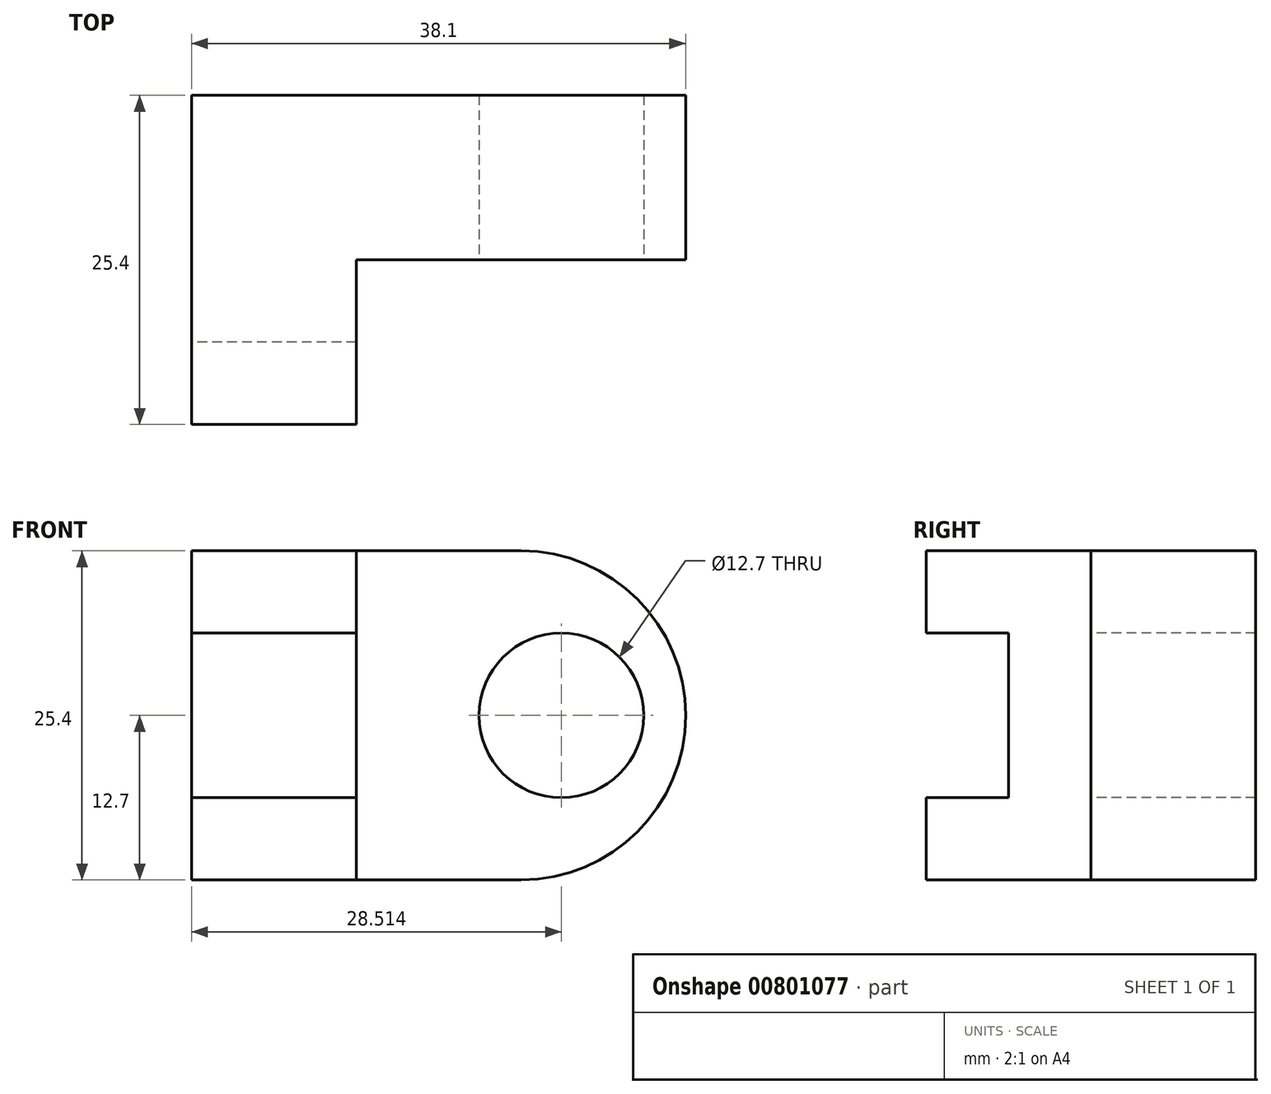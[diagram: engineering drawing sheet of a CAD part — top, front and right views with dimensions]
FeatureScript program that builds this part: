
annotation { "Feature Type Name" : "Feature", "Feature Type Description" : "" }
export const myFeature = defineFeature(function(context is Context, id is Id, definition is map)
    precondition{}
    {
        {
            var Q0;
            Q0=qCreatedBy(makeId("Front.planeOp"),FACE);
            var sketch = newSketch(context, id + "F0", { "sketchPlane" : qUnion([Q0])});
            skLineSegment(sketch, "E0", {"start": v(0, 0) * mm, "end": v(12.7, 0) * mm});
            skLineSegment(sketch, "E1", {"start": v(0, 0) * mm, "end": v(0, 25.4) * mm});
            skLineSegment(sketch, "E2", {"start": v(12.7, 0) * mm, "end": v(12.7, 25.4) * mm});
            skLineSegment(sketch, "E3", {"start": v(12.7, 25.4) * mm, "end": v(0, 25.4) * mm});
            skSolve(sketch);
        }
        {
            var Q0;
            Q0 = qSketchRegion(id + "F0", true);
            extrude(context, id + "F1", {"entities" : qUnion([Q0]), "depth" : 25.4 * mm, "offsetDistance" : 25.4 * mm});
        }
        {
            var Q0;
            Q0=makeQuery(id+"F1.opExtrude","SWEPT_FACE",FACE,{"disambiguationData":[OSD([sQuery(id+"F0.wireOp",EDGE,"E2")])]});
            var sketch = newSketch(context, id + "F2", { "sketchPlane" : qUnion([Q0])});
            skLineSegment(sketch, "E4", {"start": v(0, 0) * mm, "end": v(-12.7, 0) * mm});
            skLineSegment(sketch, "E5", {"start": v(-12.7, 0) * mm, "end": v(-12.7, 25.4) * mm});
            skLineSegment(sketch, "E6", {"start": v(0, 0) * mm, "end": v(0, 25.4) * mm});
            skLineSegment(sketch, "E7", {"start": v(-12.7, 25.4) * mm, "end": v(0, 25.4) * mm});
            skSolve(sketch);
        }
        {
            var Q0;
            Q0 = qSketchRegion(id + "F2", true);
            extrude(context, id + "F3", {"entities" : qUnion([Q0]), "operationType" : NewBodyOperationType.ADD, "depth" : 25.4 * mm, "offsetDistance" : 25.4 * mm});
        }
        {
            var Q0;
            Q0=makeQuery(id+"F1.opExtrude","CAP_FACE",FACE,{"disambiguationData":[OSD([sQuery(id+"F0.wireOp",EDGE,"E0"),sQuery(id+"F0.wireOp",EDGE,"E1"),sQuery(id+"F0.wireOp",EDGE,"E2"),sQuery(id+"F0.wireOp",EDGE,"E3")])],"isStart":false});
            var sketch = newSketch(context, id + "F4", { "sketchPlane" : qUnion([Q0])});
            skLineSegment(sketch, "E8", {"start": v(12.7, 0) * mm, "end": v(12.7, 6.35) * mm});
            skLineSegment(sketch, "E9", {"start": v(12.7, 6.35) * mm, "end": v(0, 6.35) * mm});
            skLineSegment(sketch, "E10", {"start": v(0, 6.35) * mm, "end": v(0, 0) * mm});
            skLineSegment(sketch, "E11", {"start": v(12.7, 6.35) * mm, "end": v(12.7, 19.05) * mm});
            skLineSegment(sketch, "E12", {"start": v(12.7, 19.05) * mm, "end": v(0, 19.05) * mm});
            skSolve(sketch);
        }
        {
            var Q0;
            {var subQ0=sQuery(id+"F4.wireOp",EDGE,"E9");Q0=makeQuery(id+"F4.imprint","IMPRINT",FACE,{"disambiguationData":[TD([[makeQuery(id+"F4.imprint","IMPRINT",EDGE,{"derivedFrom":subQ0}),-1.0]])]});}
            extrude(context, id + "F5", {"entities" : qUnion([Q0]), "operationType" : NewBodyOperationType.REMOVE, "oppositeDirection" : true, "depth" : 6.35 * mm, "offsetDistance" : 25.4 * mm});
        }
        {
            var Q0;
            Q0=makeQuery(id+"F3.opExtrude","SWEPT_FACE",FACE,{"disambiguationData":[OSD([sQuery(id+"F2.wireOp",EDGE,"E5")])]});
            var sketch = newSketch(context, id + "F6", { "sketchPlane" : qUnion([Q0])});
            skLineSegment(sketch, "E13", {"start": v(12.7, 25.4) * mm, "end": v(25.4, 25.4) * mm});
            skLineSegment(sketch, "E14", {"start": v(12.7, 0) * mm, "end": v(25.4, 0) * mm});
            skArc(sketch, "E15", {"start": v(25.4, 0) * mm, "mid": v(38.1, 12.7) * mm, "end": v(25.4, 25.4) * mm});
            skSolve(sketch);
        }
        {
            var Q0;
            {var subQ0=sQuery(id+"F6.wireOp",EDGE,"E15");var subQ1=sQuery(id+"F2.wireOp",EDGE,"E5");var subQ4=makeQuery(id+"F3.opExtrude","CAP_EDGE",EDGE,{"disambiguationData":[OSD([subQ1])],"isStart":false});var subQ5=makeQuery(id+"F6.imprint","INTERSECT",VERTEX,{"derivedFrom":[subQ4,subQ0]});Q0=makeQuery(id+"F6.imprint","IMPRINT",FACE,{"disambiguationData":[TD([[makeQuery(id+"F6.imprint","IMPRINT",EDGE,{"disambiguationData":[TD([[subQ5,-1.0]])],"derivedFrom":subQ4}),1.0]])]});}
            var Q1;
            {var subQ0=sQuery(id+"F6.wireOp",EDGE,"E15");var subQ1=sQuery(id+"F2.wireOp",EDGE,"E5");var subQ4=makeQuery(id+"F3.opExtrude","CAP_EDGE",EDGE,{"disambiguationData":[OSD([subQ1])],"isStart":false});var subQ5=makeQuery(id+"F6.imprint","INTERSECT",VERTEX,{"derivedFrom":[subQ4,subQ0]});Q1=makeQuery(id+"F6.imprint","IMPRINT",FACE,{"disambiguationData":[TD([[makeQuery(id+"F6.imprint","IMPRINT",EDGE,{"disambiguationData":[TD([[subQ5,1.0]])],"derivedFrom":subQ4}),1.0]])]});}
            extrude(context, id + "F7", {"entities" : qUnion([Q0, Q1]), "operationType" : NewBodyOperationType.REMOVE, "oppositeDirection" : true, "depth" : 25.4 * mm, "offsetDistance" : 25.4 * mm});
        }
        {
            var Q0;
            Q0=makeQuery(id+"F3.opExtrude","SWEPT_FACE",FACE,{"disambiguationData":[OSD([sQuery(id+"F2.wireOp",EDGE,"E5")])]});
            var sketch = newSketch(context, id + "F8", { "sketchPlane" : qUnion([Q0])});
            skCircle(sketch, "E16", {"center": v(28.51, 12.7) * mm, "radius": 6.35 * mm});
            skPoint(sketch, "E16.centerSnap0", {"position": v(12.7, 12.7) * mm});
            skSolve(sketch);
        }
        {
            var Q0;
            Q0=makeQuery(id+"F8.imprint","IMPRINT",FACE,{"disambiguationData":[TD([[makeQuery(id+"F8.imprint","IMPRINT",EDGE,{"derivedFrom":sQuery(id+"F8.wireOp",EDGE,"E16")}),1.0]])]});
            extrude(context, id + "F9", {"entities" : qUnion([Q0]), "operationType" : NewBodyOperationType.REMOVE, "endBound" : BoundingType.UP_TO_NEXT, "oppositeDirection" : true, "depth" : 25.4 * mm, "offsetDistance" : 25.4 * mm});
        }
    });
